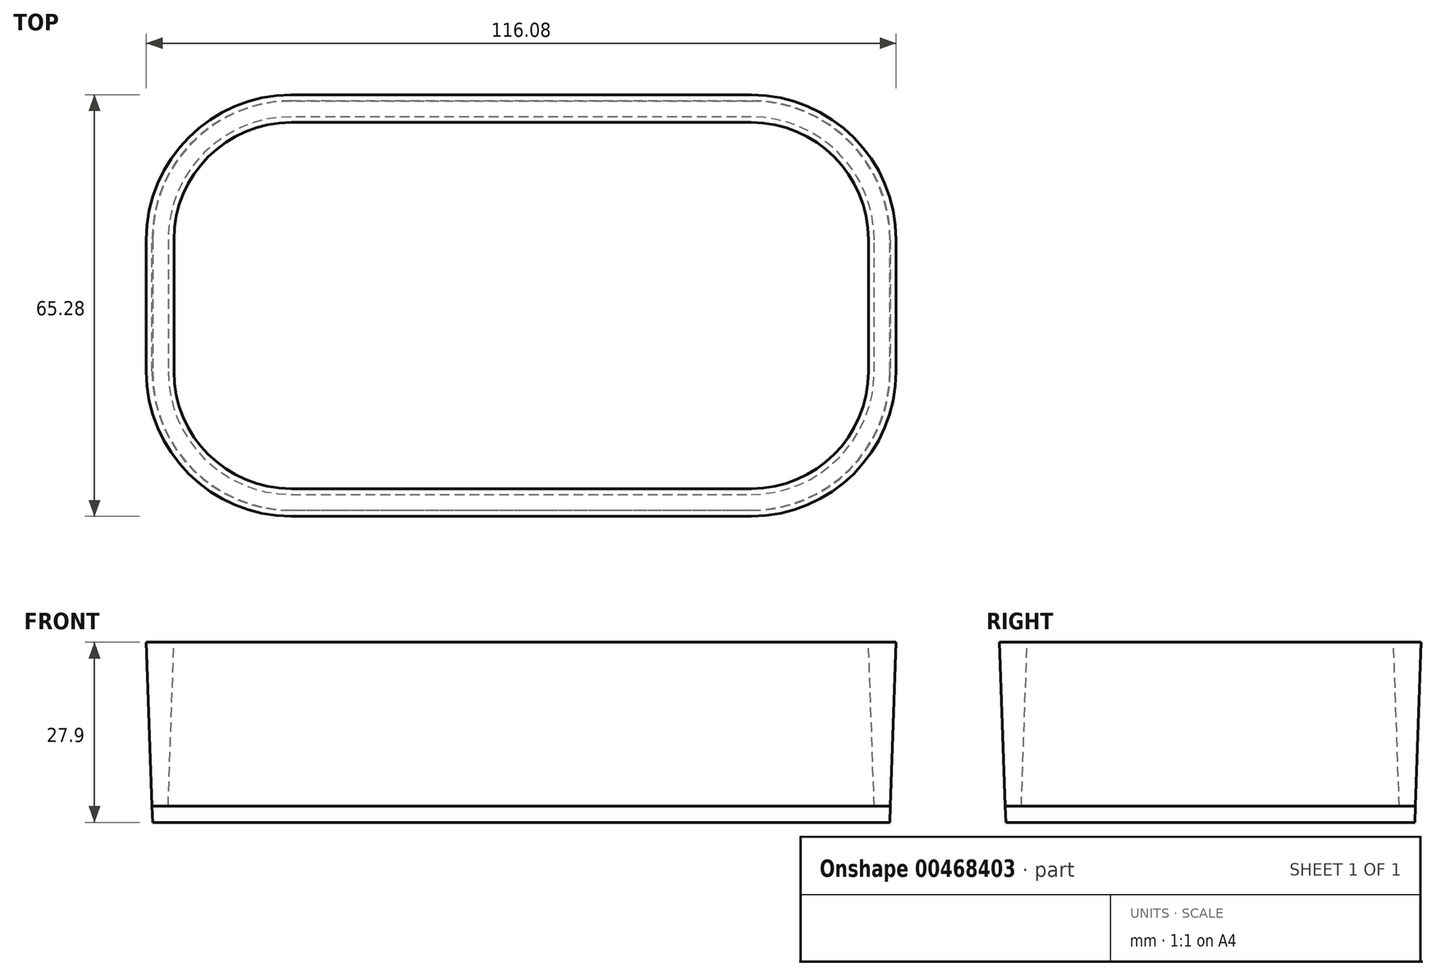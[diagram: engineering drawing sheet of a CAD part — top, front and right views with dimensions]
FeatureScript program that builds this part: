
annotation { "Feature Type Name" : "Feature", "Feature Type Description" : "" }
export const myFeature = defineFeature(function(context is Context, id is Id, definition is map)
    precondition{}
    {
        {
            var Q0;
            Q0=qCreatedBy(makeId("Top.planeOp"),FACE);
            var sketch = newSketch(context, id + "F0", { "sketchPlane" : qUnion([Q0])});
            skLineSegment(sketch, "E0.bottom", {"start": v(38.1, -25.4) * mm, "end": v(-38.1, -25.4) * mm});
            skLineSegment(sketch, "E0.top", {"start": v(38.1, 25.4) * mm, "end": v(-38.1, 25.4) * mm});
            skLineSegment(sketch, "E0.left", {"start": v(38.1, -25.4) * mm, "end": v(38.1, 25.4) * mm});
            skLineSegment(sketch, "E0.right", {"start": v(-38.1, -25.4) * mm, "end": v(-38.1, 25.4) * mm});
            skPoint(sketch, "E0.middle", {"position": v(0, 0) * mm});
            skSolve(sketch);
        }
        {
            var Q0;
            Q0=qCreatedBy(makeId("Top.planeOp"),FACE);
            var sketch = newSketch(context, id + "F1", { "sketchPlane" : qUnion([Q0])});
            skLineSegment(sketch, "E1.bottom", {"start": v(35.6, -31.75) * mm, "end": v(-35.6, -31.75) * mm});
            skLineSegment(sketch, "E1.top", {"start": v(35.6, 31.75) * mm, "end": v(-35.6, 31.75) * mm});
            skLineSegment(sketch, "E1.left", {"start": v(57.15, -10.2) * mm, "end": v(57.15, 10.2) * mm});
            skLineSegment(sketch, "E1.right", {"start": v(-57.15, -10.2) * mm, "end": v(-57.15, 10.2) * mm});
            skPoint(sketch, "E1.middle", {"position": v(0, 0) * mm});
            skLineSegment(sketch, "E2.bottom", {"start": v(35.6, -29.25) * mm, "end": v(-35.6, -29.25) * mm});
            skLineSegment(sketch, "E2.top", {"start": v(35.6, 29.25) * mm, "end": v(-35.6, 29.25) * mm});
            skLineSegment(sketch, "E2.left", {"start": v(54.65, -10.2) * mm, "end": v(54.65, 10.2) * mm});
            skLineSegment(sketch, "E2.right", {"start": v(-54.65, -10.2) * mm, "end": v(-54.65, 10.2) * mm});
            skPoint(sketch, "E3.visualSharp", {"position": v(-54.65, 29.25) * mm});
            skArc(sketch, "E3.filletArc", {"start": v(-35.6, 29.25) * mm, "mid": v(-49.07, 23.67) * mm, "end": v(-54.65, 10.2) * mm});
            skPoint(sketch, "E4.visualSharp", {"position": v(-54.65, -29.25) * mm});
            skArc(sketch, "E4.filletArc", {"start": v(-54.65, -10.2) * mm, "mid": v(-49.07, -23.67) * mm, "end": v(-35.6, -29.25) * mm});
            skPoint(sketch, "E5.visualSharp", {"position": v(54.65, 29.25) * mm});
            skArc(sketch, "E5.filletArc", {"start": v(54.65, 10.2) * mm, "mid": v(49.07, 23.67) * mm, "end": v(35.6, 29.25) * mm});
            skPoint(sketch, "E6.visualSharp", {"position": v(54.65, -29.25) * mm});
            skArc(sketch, "E6.filletArc", {"start": v(35.6, -29.25) * mm, "mid": v(49.07, -23.67) * mm, "end": v(54.65, -10.2) * mm});
            skPoint(sketch, "E7.visualSharp", {"position": v(-57.15, -31.75) * mm});
            skArc(sketch, "E7.filletArc", {"start": v(-57.15, -10.2) * mm, "mid": v(-50.84, -25.44) * mm, "end": v(-35.6, -31.75) * mm});
            skPoint(sketch, "E8.visualSharp", {"position": v(57.15, -31.75) * mm});
            skArc(sketch, "E8.filletArc", {"start": v(35.6, -31.75) * mm, "mid": v(50.84, -25.44) * mm, "end": v(57.15, -10.2) * mm});
            skPoint(sketch, "E9.visualSharp", {"position": v(57.15, 31.75) * mm});
            skArc(sketch, "E9.filletArc", {"start": v(57.15, 10.2) * mm, "mid": v(50.84, 25.44) * mm, "end": v(35.6, 31.75) * mm});
            skPoint(sketch, "E10.visualSharp", {"position": v(-57.15, 31.75) * mm});
            skArc(sketch, "E10.filletArc", {"start": v(-35.6, 31.75) * mm, "mid": v(-50.84, 25.44) * mm, "end": v(-57.15, 10.2) * mm});
            skSolve(sketch);
        }
        {
            var Q0;
            Q0=makeQuery(id+"F1.imprint","IMPRINT",FACE,{"disambiguationData":[TD([[makeQuery(id+"F1.imprint","IMPRINT",EDGE,{"derivedFrom":sQuery(id+"F1.wireOp",EDGE,"E1.bottom")}),-1.0]])]});
            extrude(context, id + "F2", {"entities" : qUnion([Q0]), "depth" : 25.4 * mm, "hasDraft" : true, "draftAngle" : 2 * degree});
        }
        {
            var Q0;
            Q0=qCreatedBy(makeId("Top.planeOp"),FACE);
            var sketch = newSketch(context, id + "F3", { "sketchPlane" : qUnion([Q0])});
            skLineSegment(sketch, "E11.bottom", {"start": v(35.6, -31.75) * mm, "end": v(-35.6, -31.75) * mm});
            skLineSegment(sketch, "E11.top", {"start": v(35.6, 31.75) * mm, "end": v(-35.6, 31.75) * mm});
            skLineSegment(sketch, "E11.left", {"start": v(57.15, -10.2) * mm, "end": v(57.15, 10.2) * mm});
            skLineSegment(sketch, "E11.right", {"start": v(-57.15, -10.2) * mm, "end": v(-57.15, 10.2) * mm});
            skPoint(sketch, "E11.middle", {"position": v(0, 0) * mm});
            skPoint(sketch, "E12.visualSharp", {"position": v(-54.65, 29.25) * mm});
            skPoint(sketch, "E13.visualSharp", {"position": v(-54.65, -29.25) * mm});
            skPoint(sketch, "E14.visualSharp", {"position": v(54.65, 29.25) * mm});
            skPoint(sketch, "E15.visualSharp", {"position": v(54.65, -29.25) * mm});
            skPoint(sketch, "E16.visualSharp", {"position": v(-57.15, -31.75) * mm});
            skArc(sketch, "E16.filletArc", {"start": v(-57.15, -10.2) * mm, "mid": v(-50.84, -25.44) * mm, "end": v(-35.6, -31.75) * mm});
            skPoint(sketch, "E17.visualSharp", {"position": v(57.15, -31.75) * mm});
            skArc(sketch, "E17.filletArc", {"start": v(35.6, -31.75) * mm, "mid": v(50.84, -25.44) * mm, "end": v(57.15, -10.2) * mm});
            skPoint(sketch, "E18.visualSharp", {"position": v(57.15, 31.75) * mm});
            skArc(sketch, "E18.filletArc", {"start": v(57.15, 10.2) * mm, "mid": v(50.84, 25.44) * mm, "end": v(35.6, 31.75) * mm});
            skPoint(sketch, "E19.visualSharp", {"position": v(-57.15, 31.75) * mm});
            skArc(sketch, "E19.filletArc", {"start": v(-35.6, 31.75) * mm, "mid": v(-50.84, 25.44) * mm, "end": v(-57.15, 10.2) * mm});
            skSolve(sketch);
        }
        {
            var Q0;
            Q0=makeQuery(id+"F3.imprint","IMPRINT",FACE,{"disambiguationData":[TD([[makeQuery(id+"F3.imprint","IMPRINT",EDGE,{"derivedFrom":sQuery(id+"F3.wireOp",EDGE,"E11.bottom")}),-1.0]])]});
            extrude(context, id + "F4", {"entities" : qUnion([Q0]), "oppositeDirection" : true, "depth" : 2.5 * mm, "hasDraft" : true, "draftAngle" : 2 * degree, "draftPullDirection" : true});
        }
    });
